# Revit family: URAN
name_source: partatom
category: Осветительные приборы
revit_build: Autodesk Revit 2016 (Build: 20151007_0715(x64)
units: mm (PartAtom-declared; Revit-internal decimal feet)

## family parameters
Источник света = Да
Общий = Нет
Основа = Грань
При загрузке вырезать с полостями = Да
Размер круглого соединителя = Использовать диаметр
Тип детали = Нормальный
Точка расчета площади = Нет

## types (11) — shared parameters
ADSK_Единица измерения = Шт.
ADSK_Завод-изготовитель = ГК «Вартон»
ADSK_Количество фаз = 1
ADSK_Количество фаз числовое = 1
ADSK_Коэффициент мощности = 0.97
ADSK_Напряжение = 220 В
ADSK_Номинальная мощность = 0 кВт
ADSK_Полная мощность = 0 кВ·А
ADSK_Размер_Высота = 80 мм
ADSK_Размер_Ширина = 211 мм
ADSK_Энергоэффективность = 0 лм/Вт
IP Class = IP20
URL = http://varton.ru
Блок аварийного питания = Нет
Видимая форма излучения при визуализации = Нет
Группа модели = Светильники
Изготовитель = ГК «Вартон»
Излучение по ширине прямоугольника = 211 мм
Класс Защиты = I
Класс пожароопасности = нет
Климатическая зона = УХЛ4
Корпус = ABS-пластик
Область использования = Уличное освещение
Плафон = Плафон самосвечение
Полная установленная мощность = 0 кВ·А
Разработчик = ООО ПРОРУБИМ
Разработчик (телефон) = +7 (495) 649-85-43
Разработчик модели (URL) = http://prorubim.com
Светофильтр = 16777215
Смещение цветовой температуры при затухании лампы = <Нет>
Тип ИС = LED
Угол наклона = -90.00°
Файл фотометрической сетки = V1-S1-70088-40L04-6509050-29104.ies
zero-valued in all types: Отметка по умолчанию

## per-type parameters (varying)
| type | ADSK_Масса | ADSK_Наименование | ADSK_Размер_Длина | ADSK_Ток | Излучение по длине прямоугольника | Массив | Описание | Тип продукции |
| V1-S1-70087-40L04-6506050 | 5.2 | Светодиодный светильник ВАРТОН уличный Uran крепление на консоль  390 x 211 х 80 мм 60Вт 5000К | 390 мм | 0 А | 390 мм | 3 | Светодиодный светильник ВАРТОН уличный Uran крепление на консоль  390 x 211 х 80 мм 60Вт 5000К | Светодиодный светильник ВАРТОН уличный Uran крепление на консоль  390 x 211 х 80 мм 60Вт 5000К |
| V1-S1-70088-40L04-6509050 | 5.7 | Светодиодный светильник ВАРТОН уличный Uran крепление на консоль  390 x 211 х 80 мм 90Вт 5000К | 390 мм | 0 А | 390 мм | 3 | Светодиодный светильник ВАРТОН уличный Uran крепление на консоль  390 x 211 х 80 мм 90Вт 5000К | Светодиодный светильник ВАРТОН уличный Uran крепление на консоль  390 x 211 х 80 мм 90Вт 5000К |
| V1-S1-70089-40L04-6512050 | 6 | Светодиодный светильник ВАРТОН уличный Uran крепление на консоль  390 x 211 х 80 мм 120Вт 5000К | 390 мм | 1 А | 390 мм | 3 | Светодиодный светильник ВАРТОН уличный Uran крепление на консоль  390 x 211 х 80 мм 120Вт 5000К | Светодиодный светильник ВАРТОН уличный Uran крепление на консоль  390 x 211 х 80 мм 120Вт 5000К |
| V1-S1-70090-40L04-6515050 | 6.3 | Светодиодный светильник ВАРТОН уличный Uran крепление на консоль  510 x 211 х 80 мм 150Вт 5000К | 510 мм | 1 А | 510 мм | 4 | Светодиодный светильник ВАРТОН уличный Uran крепление на консоль  510 x 211 х 80 мм 150Вт 5000К | Светодиодный светильник ВАРТОН уличный Uran крепление на консоль  510 x 211 х 80 мм 150Вт 5000К |
| V1-S1-70091-40L04-6518050 | 7 | Светодиодный светильник ВАРТОН уличный Uran крепление на консоль  664 x 211 х 80 мм 180Вт 5000К | 664 мм | 1 А | 664 мм | 5 | Светодиодный светильник ВАРТОН уличный Uran крепление на консоль  664 x 211 х 80 мм 180Вт 5000К | Светодиодный светильник ВАРТОН уличный Uran крепление на консоль  664 x 211 х 80 мм 180Вт 5000К |
| V1-S1-70117-40L04-6525050 | 7.5 | Светодиодный светильник ВАРТОН уличный Uran крепление на консоль  704 x 211 х 80 мм 250Вт 5000К | 704 мм | 1 А | 704 мм | 5 | Светодиодный светильник ВАРТОН уличный Uran крепление на консоль  704 x 211 х 80 мм 250Вт 5000К | Светодиодный светильник ВАРТОН уличный Uran крепление на консоль  704 x 211 х 80 мм 250Вт 5000К |
| V1-S1-70087-40L04-6506030 | 5.2 | Светодиодный светильник ВАРТОН уличный Uran крепление на консоль  390 x 211 х 80 мм 60Вт 3000К | 390 мм | 0 А | 390 мм | 3 | Светодиодный светильник ВАРТОН уличный Uran крепление на консоль  390 x 211 х 80 мм 60Вт 3000К | Светодиодный светильник ВАРТОН уличный Uran крепление на консоль  390 x 211 х 80 мм 60Вт 3000К |
| V1-S1-70088-40L04-6509030 | 5.7 | Светодиодный светильник ВАРТОН уличный Uran крепление на консоль  390 x 211 х 80 мм 90Вт 3000К | 390 мм | 0 А | 390 мм | 3 | Светодиодный светильник ВАРТОН уличный Uran крепление на консоль  390 x 211 х 80 мм 90Вт 3000К | Светодиодный светильник ВАРТОН уличный Uran крепление на консоль  390 x 211 х 80 мм 90Вт 3000К |
| V1-S1-70089-40L04-6512030 | 6 | Светодиодный светильник ВАРТОН уличный Uran крепление на консоль  390 x 211 х 80 мм 120Вт 3000К | 390 мм | 1 А | 390 мм | 3 | Светодиодный светильник ВАРТОН уличный Uran крепление на консоль  390 x 211 х 80 мм 120Вт 3000К | Светодиодный светильник ВАРТОН уличный Uran крепление на консоль  390 x 211 х 80 мм 120Вт 3000К |
| V1-S1-70090-40L04-6515030 | 6.3 | Светодиодный светильник ВАРТОН уличный Uran крепление на консоль  510 x 211 х 80 мм 150Вт 3000К | 510 мм | 1 А | 510 мм | 4 | Светодиодный светильник ВАРТОН уличный Uran крепление на консоль  510 x 211 х 80 мм 150Вт 3000К | Светодиодный светильник ВАРТОН уличный Uran крепление на консоль  510 x 211 х 80 мм 150Вт 3000К |
| V1-S1-70091-40L04-6518030 | 7 | Светодиодный светильник ВАРТОН уличный Uran крепление на консоль  664 x 211 х 80 мм 180Вт 3000К | 664 мм | 1 А | 664 мм | 5 | Светодиодный светильник ВАРТОН уличный Uran крепление на консоль  664 x 211 х 80 мм 180Вт 3000К | Светодиодный светильник ВАРТОН уличный Uran крепление на консоль  664 x 211 х 80 мм 180Вт 3000К |

note: column(s) folded — value = type name in every type: ADSK_Код изделия

## geometry (parser evidence)
native form markers: Blend x2
no freeform markers — native parametric forms only
